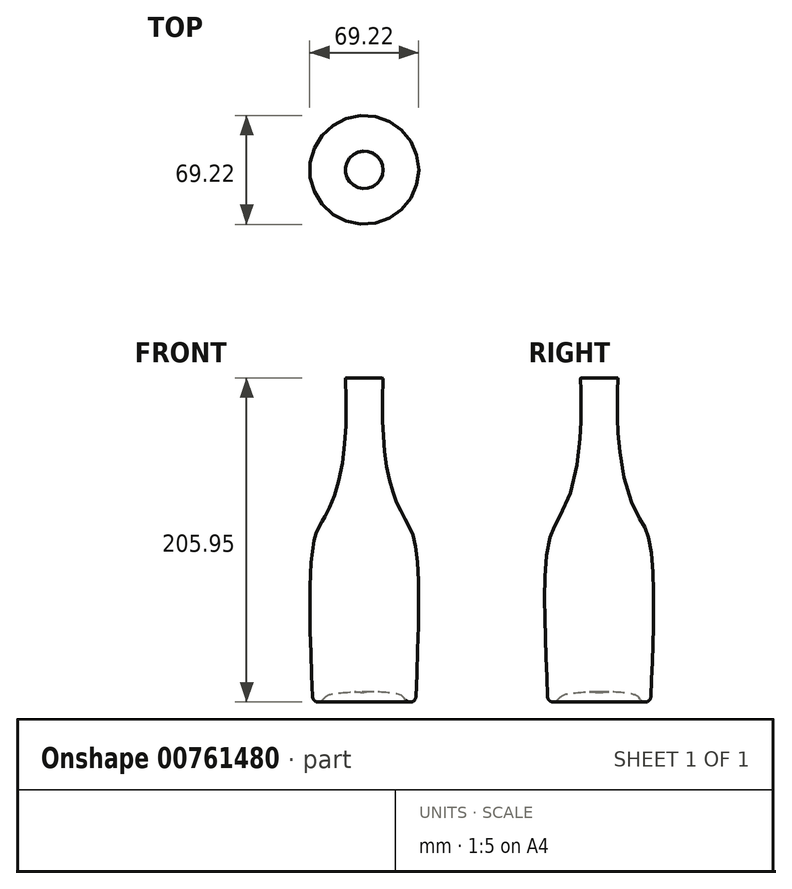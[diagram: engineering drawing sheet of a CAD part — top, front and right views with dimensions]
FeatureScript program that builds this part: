
annotation { "Feature Type Name" : "Feature", "Feature Type Description" : "" }
export const myFeature = defineFeature(function(context is Context, id is Id, definition is map)
    precondition{}
    {
        {
            var Q0;
            Q0=qCreatedBy(makeId("Front.planeOp"),FACE);
            var sketch = newSketch(context, id + "F0", { "sketchPlane" : qUnion([Q0])});
            skLineSegment(sketch, "E0", {"start": v(0, 0) * mm, "end": v(0, 210) * mm});
            skFitSpline(sketch, "E1", {"points": [v(32.58, 0.03) * mm, v(32.58, 101.84) * mm, v(24.8, 120.8) * mm, v(15.65, 144.91) * mm, v(11.45, 193.04) * mm, v(11.87, 208.2) * mm, v(11.69, 208.36) * mm, v(0, 208.19) * mm], "startDerivative": vector(13.13, 344.54) * mm, "endDerivative": vector(-160.7, 1.55) * mm});
            skPoint(sketch, "E2", {"position": v(11.45, 193.36) * mm});
            skFitSpline(sketch, "E3", {"points": [v(32.58, 0.03) * mm, v(24.8, 5.64) * mm, v(15.88, 8.26) * mm, v(0, 8.41) * mm], "startDerivative": vector(-44.6, -0.27) * mm, "endDerivative": vector(-39.9, -7.38) * mm});
            skSolve(sketch);
        }
        {
            var Q0;
            Q0=qSketchRegion(id+"F0",true);
            var Q1;
            Q1=qConstructionFilter(qBodyType(qCreatedBy(id+"F0",EDGE),BodyType.WIRE),ConstructionObject.NO);
            var Q2;
            Q2=sQuery(id+"F0.wireOp",EDGE,"E0");
            revolve(context, id + "F1", {"surfaceOperationType" : NewSurfaceOperationType.NEW, "entities" : qUnion([Q0]), "surfaceEntities" : qUnion([Q1]), "axis" : qUnion([Q2]), "revolveType" : RevolveType.FULL});
        }
        {
            var Q0;
            Q0=qCreatedBy(makeId("Top.planeOp"),FACE);
            cPlane(context, id + "F2", {"entities" : qUnion([Q0]), "cplaneType" : CPlaneType.OFFSET, "offset" : 228 * mm, "width" : 150 * mm, "height" : 150 * mm});
        }
        {
            var Q0;
            Q0=makeQuery(id+"F1.opRevolve","SWEPT_FACE",FACE,{"disambiguationData":[OSD([sQuery(id+"F0.wireOp",EDGE,"E1")])]});
            fillet(context, id + "F3", {"entities" : qUnion([Q0]), "radius" : 3.6 * mm, "tangentPropagation" : true, "allowEdgeOverflow" : false});
        }
    });
